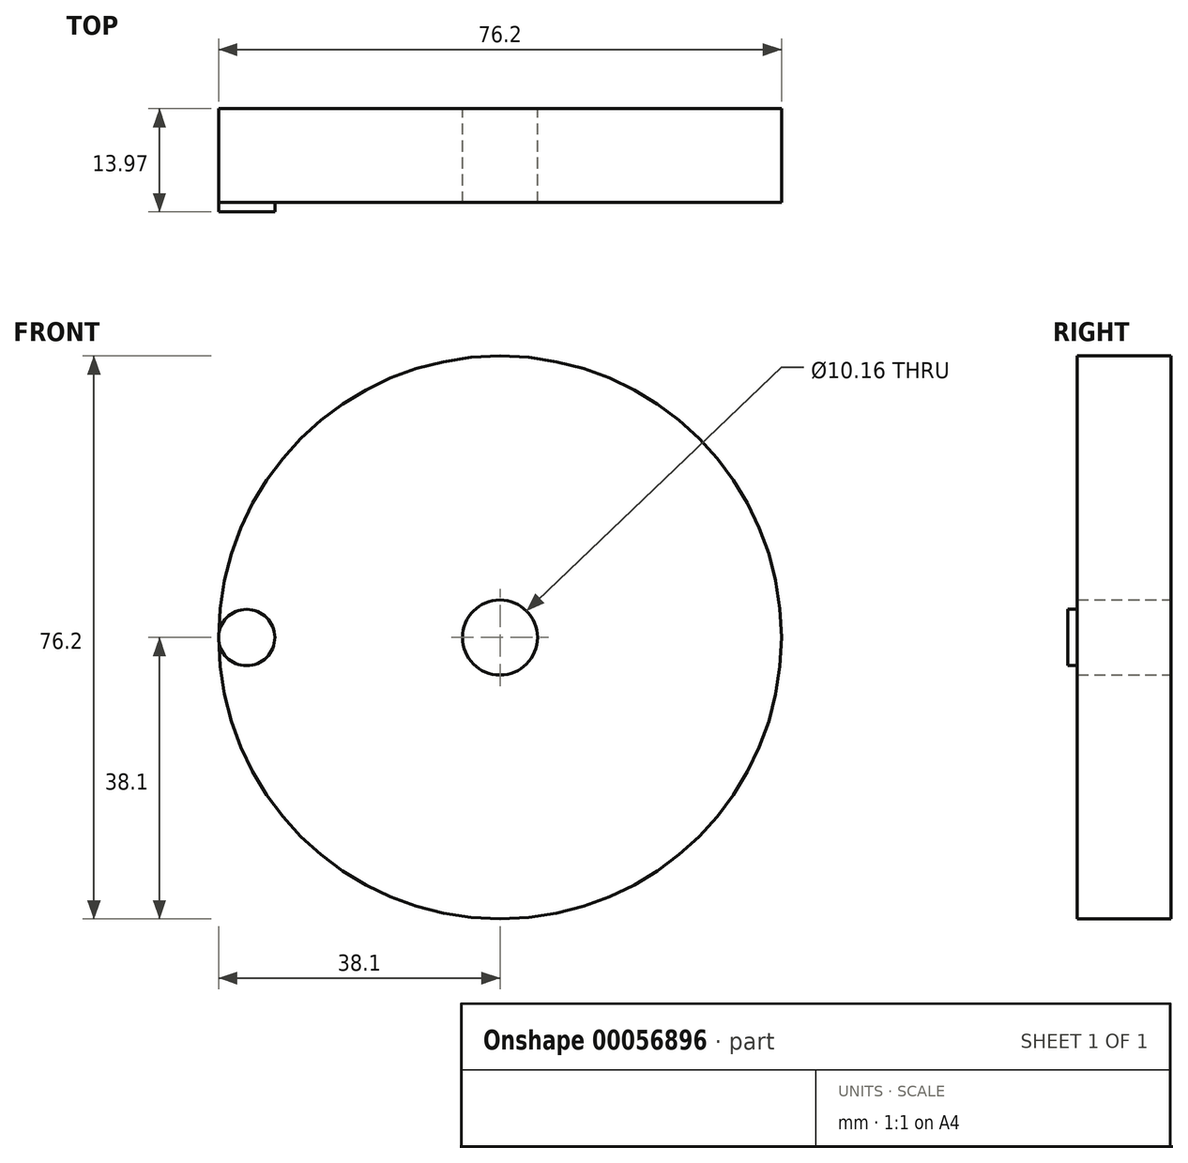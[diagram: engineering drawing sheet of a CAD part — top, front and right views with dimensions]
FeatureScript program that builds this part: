
annotation { "Feature Type Name" : "Feature", "Feature Type Description" : "" }
export const myFeature = defineFeature(function(context is Context, id is Id, definition is map)
    precondition{}
    {
        {
            var Q0;
            Q0=qCreatedBy(makeId("Front.planeOp"),FACE);
            var sketch = newSketch(context, id + "F0", { "sketchPlane" : qUnion([Q0])});
            skCircle(sketch, "E0", {"center": v(0, 0) * mm, "radius": 38.1 * mm});
            skCircle(sketch, "E1", {"center": v(-34.3, 0) * mm, "radius": 3.8 * mm});
            skCircle(sketch, "E2", {"center": v(34.3, 0) * mm, "radius": 3.8 * mm});
            skSolve(sketch);
        }
        {
            var Q0;
            Q0=makeQuery(id+"F0.imprint","IMPRINT",FACE,{"disambiguationData":[TD([[makeQuery(id+"F0.imprint","IMPRINT",EDGE,{"derivedFrom":sQuery(id+"F0.wireOp",EDGE,"E0")}),1.0]])]});
            var Q1;
            Q1=makeQuery(id+"F0.imprint","IMPRINT",FACE,{"disambiguationData":[TD([[makeQuery(id+"F0.imprint","IMPRINT",EDGE,{"derivedFrom":sQuery(id+"F0.wireOp",EDGE,"E1")}),1.0]])]});
            var Q2;
            Q2=makeQuery(id+"F0.imprint","IMPRINT",FACE,{"disambiguationData":[TD([[makeQuery(id+"F0.imprint","IMPRINT",EDGE,{"derivedFrom":sQuery(id+"F0.wireOp",EDGE,"E2")}),1.0]])]});
            extrude(context, id + "F1", {"entities" : qUnion([Q0, Q1, Q2]), "endBound" : BoundingType.SYMMETRIC, "depth" : 12.7 * mm});
        }
        {
            var Q0;
            Q0=makeQuery(id+"F1.opExtrude","CAP_FACE",FACE,{"disambiguationData":[OSD([sQuery(id+"F0.wireOp",EDGE,"E0")])],"isStart":false});
            var Q1;
            Q1=makeQuery(id+"F1.opExtrude","CAP_FACE",FACE,{"disambiguationData":[OSD([sQuery(id+"F0.wireOp",EDGE,"E0")])],"isStart":true});
            shell(context, id + "F2", {"entities" : qUnion([Q0, Q1]), "thickness" : 33.02 * mm});
        }
        {
            var Q0;
            Q0=makeQuery(id+"F0.imprint","IMPRINT",FACE,{"disambiguationData":[TD([[makeQuery(id+"F0.imprint","IMPRINT",EDGE,{"derivedFrom":sQuery(id+"F0.wireOp",EDGE,"E1")}),1.0]])]});
            extrude(context, id + "F3", {"entities" : qUnion([Q0]), "operationType" : NewBodyOperationType.ADD, "depth" : 7.62 * mm});
        }
    });
